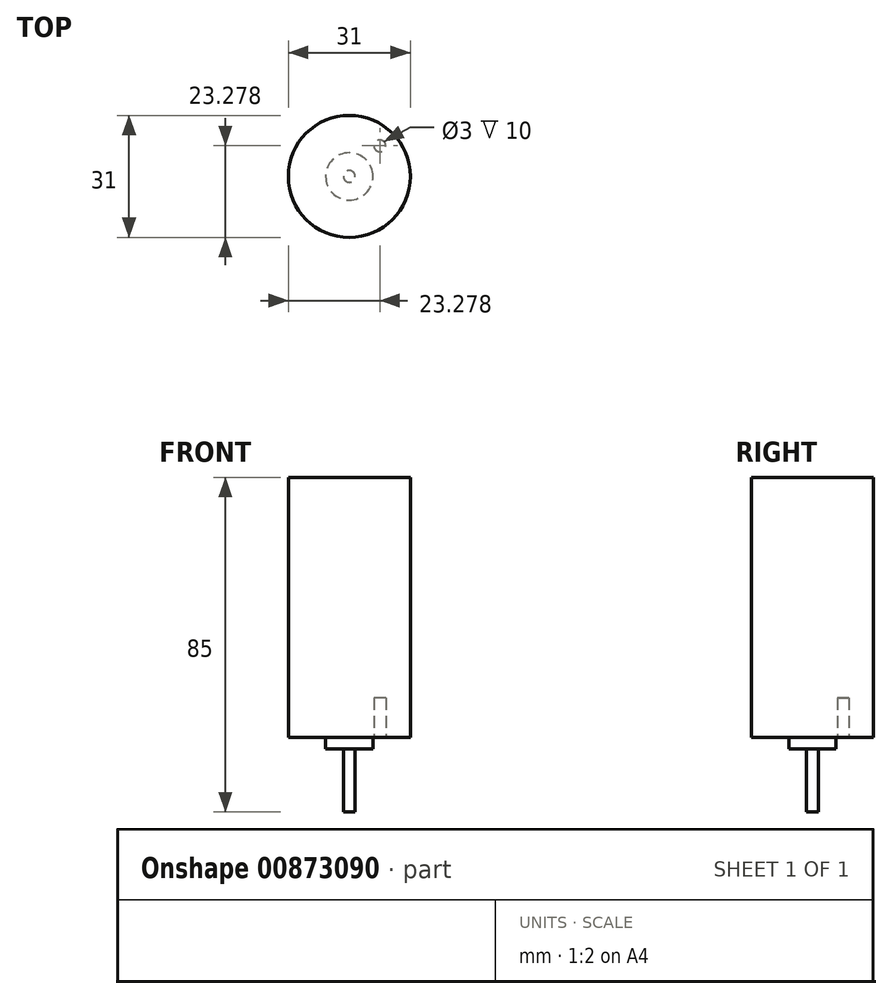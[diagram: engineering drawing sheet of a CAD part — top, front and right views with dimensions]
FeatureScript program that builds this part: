
annotation { "Feature Type Name" : "Feature", "Feature Type Description" : "" }
export const myFeature = defineFeature(function(context is Context, id is Id, definition is map)
    precondition{}
    {
        {
            var Q0;
            Q0=qCreatedBy(makeId("Top.planeOp"),FACE);
            var sketch = newSketch(context, id + "F0", { "sketchPlane" : qUnion([Q0])});
            skCircle(sketch, "E0", {"center": v(0, 0) * mm, "radius": 1.5 * mm});
            skCircle(sketch, "E1", {"center": v(0, 0) * mm, "radius": 6 * mm});
            skCircle(sketch, "E2", {"center": v(0, 0) * mm, "radius": 15.5 * mm});
            skCircle(sketch, "E3", {"center": v(0, 0) * mm, "radius": 11 * mm, "construction": true});
            skLineSegment(sketch, "E4", {"start": v(0, 0) * mm, "end": v(0, 31.33) * mm, "construction": true});
            skLineSegment(sketch, "E5", {"start": v(0, 0) * mm, "end": v(24.84, 24.84) * mm, "construction": true});
            skCircle(sketch, "E6", {"center": v(7.78, 7.78) * mm, "radius": 1.5 * mm});
            skSolve(sketch);
        }
        {
            var Q0;
            Q0=makeQuery(id+"F0.imprint","IMPRINT",FACE,{"disambiguationData":[TD([[makeQuery(id+"F0.imprint","IMPRINT",EDGE,{"derivedFrom":sQuery(id+"F0.wireOp",EDGE,"E0")}),1.0]])]});
            var Q1;
            Q1=sQuery(id+"F0.wireOp",EDGE,"E1");
            extrude(context, id + "F1", {"entities" : qUnion([Q0]), "surfaceEntities" : qUnion([Q1]), "oppositeDirection" : true, "depth" : 19 * mm, "offsetDistance" : 25 * mm});
        }
        {
            var Q0;
            Q0=makeQuery(id+"F0.imprint","IMPRINT",FACE,{"disambiguationData":[TD([[makeQuery(id+"F0.imprint","IMPRINT",EDGE,{"derivedFrom":sQuery(id+"F0.wireOp",EDGE,"E0")}),-1.0]])]});
            extrude(context, id + "F2", {"entities" : qUnion([Q0]), "operationType" : NewBodyOperationType.ADD, "oppositeDirection" : true, "depth" : 3 * mm, "offsetDistance" : 25 * mm});
        }
        {
            var Q0;
            Q0=makeQuery(id+"F0.imprint","IMPRINT",FACE,{"disambiguationData":[TD([[makeQuery(id+"F0.imprint","IMPRINT",EDGE,{"derivedFrom":sQuery(id+"F0.wireOp",EDGE,"E1")}),-1.0]])]});
            var Q1;
            Q1=makeQuery(id+"F0.imprint","IMPRINT",FACE,{"disambiguationData":[TD([[makeQuery(id+"F0.imprint","IMPRINT",EDGE,{"derivedFrom":sQuery(id+"F0.wireOp",EDGE,"E0")}),1.0]])]});
            var Q2;
            Q2=makeQuery(id+"F0.imprint","IMPRINT",FACE,{"disambiguationData":[TD([[makeQuery(id+"F0.imprint","IMPRINT",EDGE,{"derivedFrom":sQuery(id+"F0.wireOp",EDGE,"E0")}),-1.0]])]});
            var Q3;
            Q3=makeQuery(id+"F0.imprint","IMPRINT",FACE,{"disambiguationData":[TD([[makeQuery(id+"F0.imprint","IMPRINT",EDGE,{"derivedFrom":sQuery(id+"F0.wireOp",EDGE,"E6")}),1.0]])]});
            extrude(context, id + "F3", {"entities" : qUnion([Q0, Q1, Q2, Q3]), "operationType" : NewBodyOperationType.ADD, "depth" : 66 * mm, "offsetDistance" : 25 * mm});
        }
        {
            var Q0;
            Q0=makeQuery(id+"F0.imprint","IMPRINT",FACE,{"disambiguationData":[TD([[makeQuery(id+"F0.imprint","IMPRINT",EDGE,{"derivedFrom":sQuery(id+"F0.wireOp",EDGE,"E6")}),1.0]])]});
            extrude(context, id + "F4", {"entities" : qUnion([Q0]), "operationType" : NewBodyOperationType.REMOVE, "depth" : 10 * mm, "offsetDistance" : 25 * mm});
        }
    });
